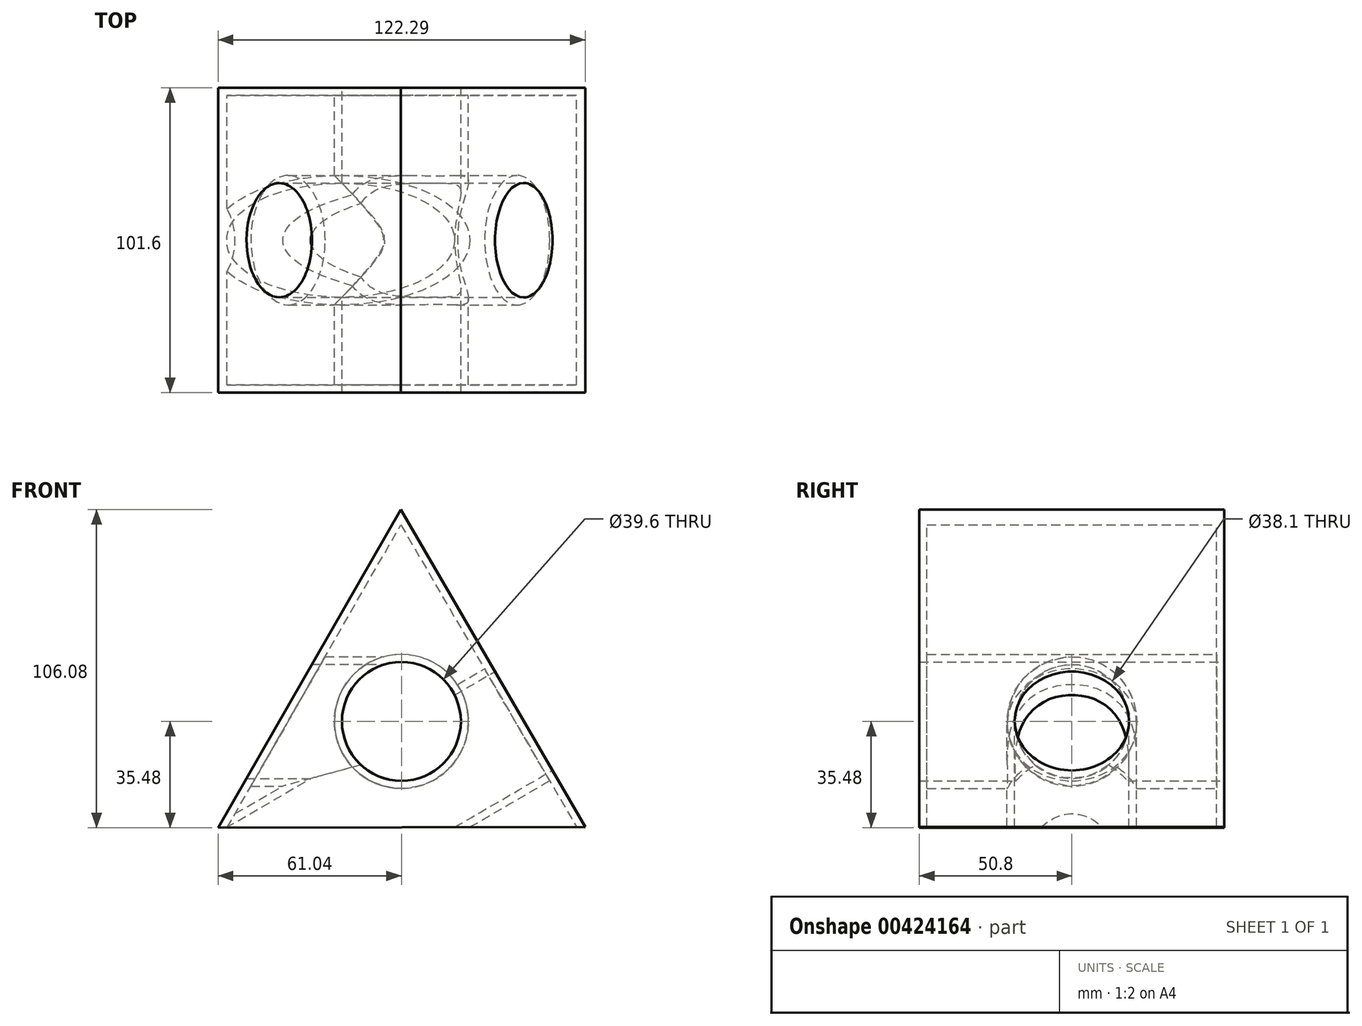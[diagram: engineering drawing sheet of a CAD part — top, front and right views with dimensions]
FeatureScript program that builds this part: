
annotation { "Feature Type Name" : "Feature", "Feature Type Description" : "" }
export const myFeature = defineFeature(function(context is Context, id is Id, definition is map)
    precondition{}
    {
        {
            var Q0;
            Q0=qCreatedBy(makeId("Front.planeOp"),FACE);
            var sketch = newSketch(context, id + "F0", { "sketchPlane" : qUnion([Q0])});
            skCircle(sketch, "E0.cCircle", {"center": v(0, 0) * mm, "radius": 35.3 * mm, "construction": true});
            skLineSegment(sketch, "E0.0", {"start": v(-61.04, -35.48) * mm, "end": v(-0.2, 70.6) * mm});
            skLineSegment(sketch, "E0.1", {"start": v(-0.2, 70.6) * mm, "end": v(61.25, -35.13) * mm});
            skLineSegment(sketch, "E0.2", {"start": v(61.25, -35.13) * mm, "end": v(-61.04, -35.48) * mm});
            skPoint(sketch, "E0.0.midPoint", {"position": v(-30.62, 17.56) * mm});
            skCircle(sketch, "E1", {"center": v(0, 0) * mm, "radius": 19.8 * mm});
            skSolve(sketch);
        }
        {
            var Q0;
            Q0=makeQuery(id+"F0.imprint","IMPRINT",FACE,{"disambiguationData":[TD([[makeQuery(id+"F0.imprint","IMPRINT",EDGE,{"derivedFrom":sQuery(id+"F0.wireOp",EDGE,"E0.0")}),-1.0]])]});
            var sketch = newSketch(context, id + "F1", { "sketchPlane" : qUnion([Q0])});
            skLineSegment(sketch, "E2", {"start": v(0, 0) * mm, "end": v(0, 70.4) * mm, "construction": true});
            skLineSegment(sketch, "E3", {"start": v(0, 0) * mm, "end": v(0, -35.58) * mm, "construction": true});
            skSolve(sketch);
        }
        {
            var Q0;
            Q0=makeQuery(id+"F0.imprint","IMPRINT",FACE,{"disambiguationData":[TD([[makeQuery(id+"F0.imprint","IMPRINT",EDGE,{"derivedFrom":sQuery(id+"F0.wireOp",EDGE,"E0.0")}),-1.0]])]});
            extrude(context, id + "F2", {"entities" : qUnion([Q0]), "depth" : 50.8 * mm});
        }
        {
            var Q0;
            Q0=makeQuery(id+"F1.imprint","IMPRINT",FACE,{"disambiguationData":[TD([[makeQuery(id+"F1.imprint","IMPRINT",EDGE,{"derivedFrom":makeQuery(id+"F0.imprint","IMPRINT",EDGE,{"derivedFrom":sQuery(id+"F0.wireOp",EDGE,"E0.0")})}),-1.0]])]});
            extrude(context, id + "F3", {"entities" : qUnion([Q0]), "operationType" : NewBodyOperationType.ADD, "depth" : 25.4 * mm});
        }
        {
            var Q0;
            Q0=makeQuery(id+"F2.opExtrude","SWEPT_BODY",BODY,{"disambiguationData":[OSD([sQuery(id+"F0.wireOp",EDGE,"E0.0"),sQuery(id+"F0.wireOp",EDGE,"E0.1"),sQuery(id+"F0.wireOp",EDGE,"E0.2"),sQuery(id+"F0.wireOp",EDGE,"E1")])]});
            var Q1;
            Q1=qCreatedBy(makeId("Front.planeOp"),FACE);
            mirror(context, id + "F4", {"operationType" : NewBodyOperationType.ADD, "entities" : qUnion([Q0]), "mirrorPlane" : qUnion([Q1])});
        }
        {
            var Q0;
            Q0=qCreatedBy(makeId("Right.planeOp"),FACE);
            var sketch = newSketch(context, id + "F5", { "sketchPlane" : qUnion([Q0])});
            skPoint(sketch, "E4", {"position": v(0, 0) * mm});
            skSolve(sketch);
        }
        {
            var Q0;
            Q0=sQuery(id+"F5.wireOp",VERTEX,"E4");
            var Q1;
            Q1=makeQuery(id+"F2.opExtrude","SWEPT_BODY",BODY,{"disambiguationData":[OSD([sQuery(id+"F0.wireOp",EDGE,"E0.0"),sQuery(id+"F0.wireOp",EDGE,"E0.1"),sQuery(id+"F0.wireOp",EDGE,"E0.2"),sQuery(id+"F0.wireOp",EDGE,"E1")])]});
            hole(context, id + "F6", {"style" : HoleStyle.SIMPLE, "endStyle" : HoleEndStyle.THROUGH, "holeDiameter" : 38.1 * mm, "isTappedThrough" : true, "tappedDepth" : 12.7 * mm, "tapClearance" : 3, "locations" : qUnion([Q0]), "scope" : qUnion([Q1])});
        }
        {
            var Q0;
            {var subQ0=makeQuery(id+"F2.opExtrude","SWEPT_FACE",FACE,{"disambiguationData":[OSD([sQuery(id+"F0.wireOp",EDGE,"E0.1")])]});Q0=makeQuery(id+"F4.boolean.opBoolean","MERGE",FACE,{"derivedFrom":[subQ0,makeQuery(id+"F4.opPattern","COPY",FACE,{"derivedFrom":subQ0,"instanceName":"1"})]});}
            var sketch = newSketch(context, id + "F7", { "sketchPlane" : qUnion([Q0])});
            skPoint(sketch, "E5", {"position": v(0, -20.34) * mm});
            skSolve(sketch);
        }
        {
            var Q0;
            Q0=sQuery(id+"F7.wireOp",VERTEX,"E5");
            var Q1;
            Q1=makeQuery(id+"F2.opExtrude","SWEPT_BODY",BODY,{"disambiguationData":[OSD([sQuery(id+"F0.wireOp",EDGE,"E0.0"),sQuery(id+"F0.wireOp",EDGE,"E0.1"),sQuery(id+"F0.wireOp",EDGE,"E0.2"),sQuery(id+"F0.wireOp",EDGE,"E1")])]});
            hole(context, id + "F8", {"style" : HoleStyle.SIMPLE, "endStyle" : HoleEndStyle.THROUGH, "holeDiameter" : 38.1 * mm, "isTappedThrough" : true, "tappedDepth" : 12.7 * mm, "tapClearance" : 3, "locations" : qUnion([Q0]), "scope" : qUnion([Q1])});
        }
        {
            var Q0;
            {var subQ0=makeQuery(id+"F2.opExtrude","SWEPT_FACE",FACE,{"disambiguationData":[OSD([sQuery(id+"F0.wireOp",EDGE,"E0.2")])]});Q0=makeQuery(id+"F4.boolean.opBoolean","MERGE",FACE,{"derivedFrom":[subQ0,makeQuery(id+"F4.opPattern","COPY",FACE,{"derivedFrom":subQ0,"instanceName":"1"})]});}
            shell(context, id + "F9", {"entities" : qUnion([Q0]), "thickness" : 2.54 * mm});
        }
    });
